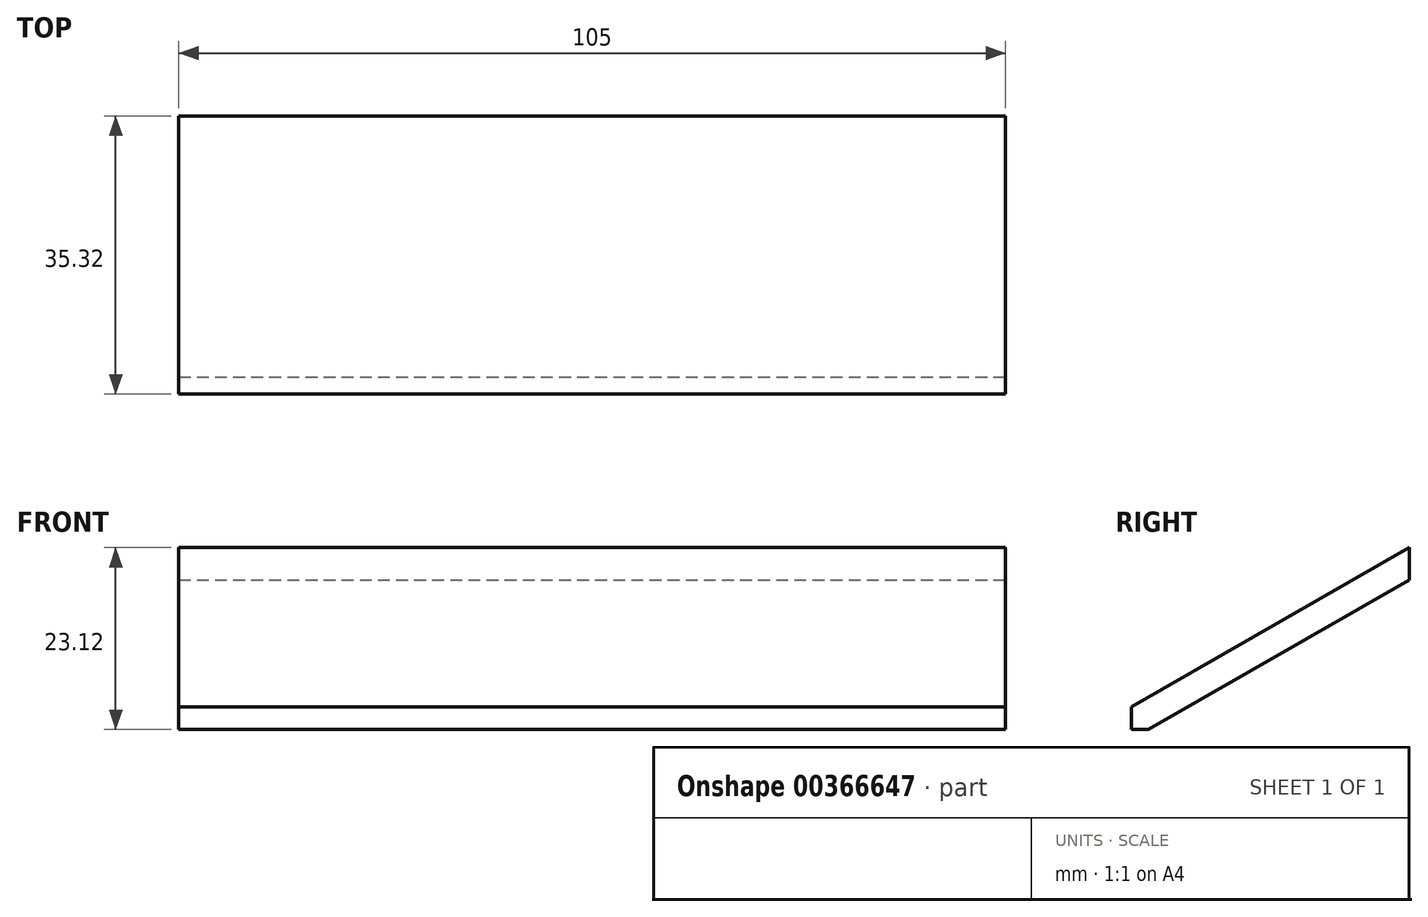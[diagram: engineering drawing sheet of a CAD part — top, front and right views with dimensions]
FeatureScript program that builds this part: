
annotation { "Feature Type Name" : "Feature", "Feature Type Description" : "" }
export const myFeature = defineFeature(function(context is Context, id is Id, definition is map)
    precondition{}
    {
        {
            var Q0;
            Q0=qCreatedBy(makeId("Top.planeOp"),FACE);
            var sketch = newSketch(context, id + "F0", { "sketchPlane" : qUnion([Q0])});
            skLineSegment(sketch, "E0.bottom", {"start": v(-53.1, 12.1) * mm, "end": v(16.9, 12.1) * mm});
            skLineSegment(sketch, "E0.top", {"start": v(-53.1, -16.85) * mm, "end": v(16.9, -16.85) * mm});
            skLineSegment(sketch, "E0.left", {"start": v(-53.1, 12.1) * mm, "end": v(-53.1, -16.85) * mm});
            skLineSegment(sketch, "E0.right", {"start": v(16.9, 12.1) * mm, "end": v(16.9, -16.85) * mm});
            skSolve(sketch);
        }
        {
            var Q0;
            Q0=makeQuery(id+"F0.imprint","IMPRINT",FACE,{"disambiguationData":[TD([[makeQuery(id+"F0.imprint","IMPRINT",EDGE,{"derivedFrom":sQuery(id+"F0.wireOp",EDGE,"E0.bottom")}),-1.0]])]});
            extrude(context, id + "F1", {"entities" : qUnion([Q0]), "depth" : 17.5 * mm});
        }
        {
            var Q0;
            Q0=makeQuery(id+"F1.opExtrude","SWEPT_FACE",FACE,{"disambiguationData":[OSD([sQuery(id+"F0.wireOp",EDGE,"E0.right")])]});
            var sketch = newSketch(context, id + "F2", { "sketchPlane" : qUnion([Q0])});
            skLineSegment(sketch, "E1", {"start": v(-16.85, 1.91) * mm, "end": v(10.35, 17.5) * mm});
            skLineSegment(sketch, "E2", {"start": v(12.1, 15.77) * mm, "end": v(-15.41, 0) * mm});
            skSolve(sketch);
        }
        {
            var Q0;
            Q0 = qSketchRegion(id + "F2", true);
            var Q1;
            {var subQ0=sQuery(id+"F2.wireOp",EDGE,"E1");Q1=makeQuery(id+"F2.imprint","IMPRINT",FACE,{"disambiguationData":[TD([[makeQuery(id+"F2.imprint","IMPRINT",EDGE,{"derivedFrom":subQ0}),1.0]])]});}
            var Q2;
            {var subQ0=sQuery(id+"F2.wireOp",EDGE,"E2");Q2=makeQuery(id+"F2.imprint","IMPRINT",FACE,{"disambiguationData":[TD([[makeQuery(id+"F2.imprint","IMPRINT",EDGE,{"derivedFrom":subQ0}),1.0]])]});}
            extrude(context, id + "F3", {"entities" : qUnion([Q0, Q1, Q2]), "operationType" : NewBodyOperationType.REMOVE, "endBound" : BoundingType.THROUGH_ALL, "oppositeDirection" : true, "depth" : 25 * mm});
        }
        {
            var Q0;
            Q0=makeQuery(id+"F1.opExtrude","SWEPT_FACE",FACE,{"disambiguationData":[OSD([sQuery(id+"F0.wireOp",EDGE,"E0.right")])]});
            var sketch = newSketch(context, id + "F4", { "sketchPlane" : qUnion([Q0])});
            skLineSegment(sketch, "E3", {"start": v(6.7, 15.4) * mm, "end": v(6.7, 12.67) * mm});
            skSolve(sketch);
        }
        {
            var Q0;
            {var subQ3=sQuery(id+"F4.wireOp",EDGE,"E3");Q0=makeQuery(id+"F4.imprint","IMPRINT",FACE,{"disambiguationData":[TD([[makeQuery(id+"F4.imprint","IMPRINT",EDGE,{"derivedFrom":subQ3}),1.0]])]});}
            extrude(context, id + "F5", {"entities" : qUnion([Q0]), "operationType" : NewBodyOperationType.REMOVE, "endBound" : BoundingType.THROUGH_ALL, "oppositeDirection" : true, "depth" : 25 * mm});
        }
        {
            var Q0;
            Q0=makeQuery(id+"F1.opExtrude","SWEPT_BODY",BODY,{"disambiguationData":[OSD([sQuery(id+"F0.wireOp",EDGE,"E0.bottom"),sQuery(id+"F0.wireOp",EDGE,"E0.top"),sQuery(id+"F0.wireOp",EDGE,"E0.left"),sQuery(id+"F0.wireOp",EDGE,"E0.right")])]});
            var Q1;
            Q1=makeQuery(id+"F3.boolean.opBoolean","COPY",VERTEX,{"derivedFrom":makeQuery(id+"F3.opExtrude","CAP_VERTEX",VERTEX,{"disambiguationData":[OSD([sQuery(id+"F0.wireOp",EDGE,"E0.top"),sQuery(id+"F0.wireOp",EDGE,"E0.right"),sQuery(id+"F2.wireOp",EDGE,"E1")])],"isStart":true})});
            transform(context, id + "F6", {"entities" : qUnion([Q0]), "transformType" : TransformType.SCALE_UNIFORMLY, "scale" : 1.5, "scalePoint" : qUnion([Q1]), "makeCopy" : false});
        }
    });
